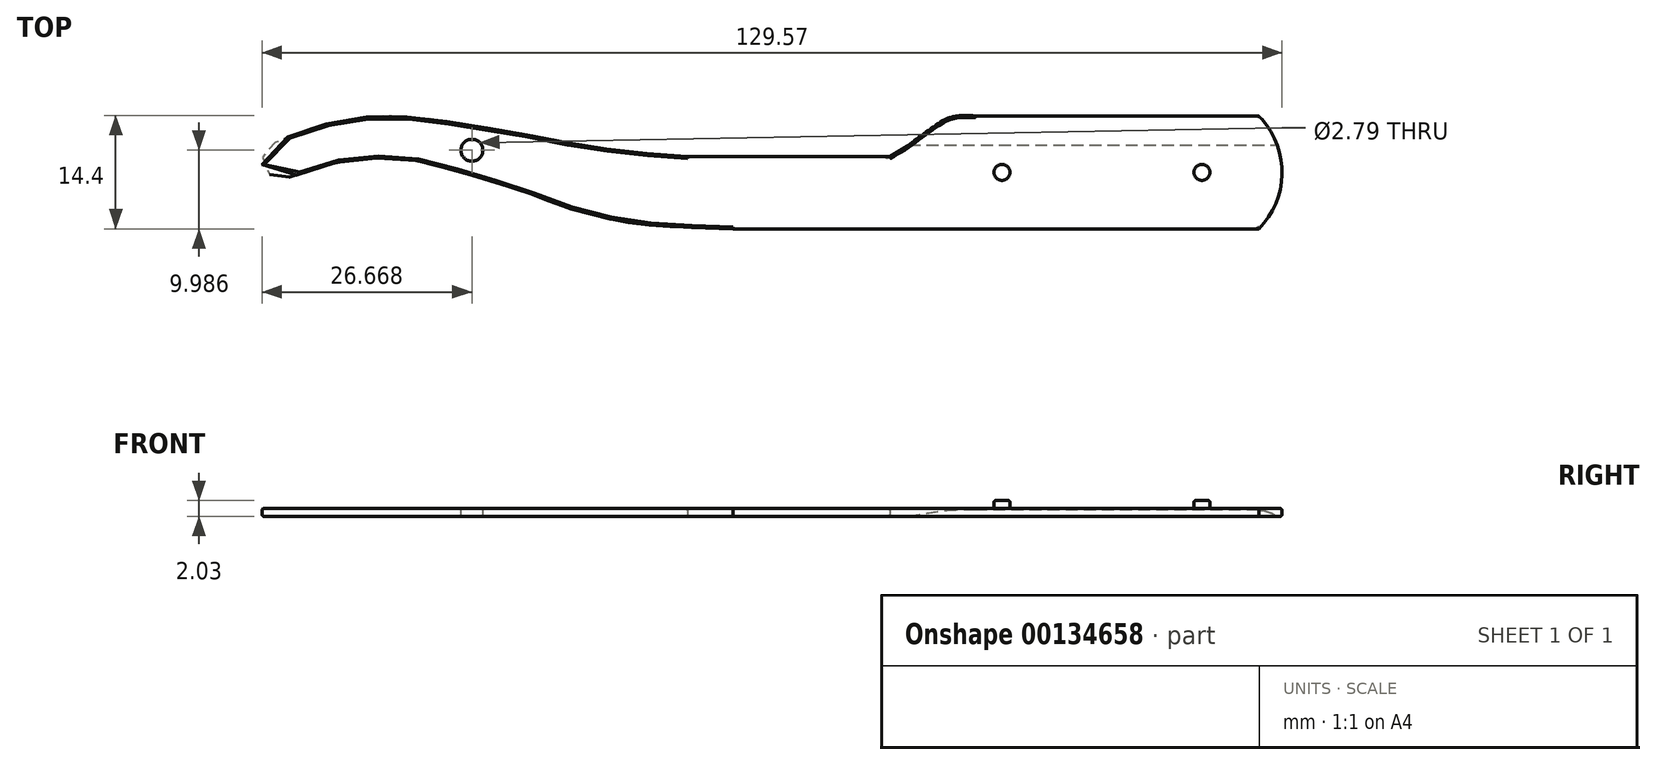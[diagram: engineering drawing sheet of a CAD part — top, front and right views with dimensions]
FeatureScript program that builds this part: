
annotation { "Feature Type Name" : "Feature", "Feature Type Description" : "" }
export const myFeature = defineFeature(function(context is Context, id is Id, definition is map)
    precondition{}
    {
        {
            var Q0;
            Q0=qCreatedBy(makeId("Top.planeOp"),FACE);
            var sketch = newSketch(context, id + "F0", { "sketchPlane" : qUnion([Q0])});
            skPoint(sketch, "E0", {"position": v(130.8, 0) * mm});
            skPoint(sketch, "E1", {"position": v(-103.94, -143.52) * mm});
            skPoint(sketch, "E2", {"position": v(0.55, 0.24) * mm});
            skPoint(sketch, "E3", {"position": v(0.4, 1.22) * mm});
            skPoint(sketch, "E4", {"position": v(0.7, 2.2) * mm});
            skPoint(sketch, "E5", {"position": v(1.36, 2.96) * mm});
            skPoint(sketch, "E6", {"position": v(5, 4.63) * mm});
            skPoint(sketch, "E7", {"position": v(9.58, 5.96) * mm});
            skPoint(sketch, "E8", {"position": v(14.71, 6.72) * mm});
            skPoint(sketch, "E9", {"position": v(19.41, 6.61) * mm});
            skPoint(sketch, "E10", {"position": v(22.67, 6.26) * mm});
            skPoint(sketch, "E11", {"position": v(23.56, 6.1) * mm});
            skPoint(sketch, "E12", {"position": v(33.06, 4.54) * mm});
            skPoint(sketch, "E13", {"position": v(37.97, 3.6) * mm});
            skPoint(sketch, "E14", {"position": v(42.95, 2.72) * mm});
            skPoint(sketch, "E15", {"position": v(46.9, 2.26) * mm});
            skPoint(sketch, "E16", {"position": v(51.6, 1.8) * mm});
            skPoint(sketch, "E17", {"position": v(54.47, 1.63) * mm});
            skPoint(sketch, "E18", {"position": v(80.16, 1.63) * mm});
            skPoint(sketch, "E19", {"position": v(82.68, 3.16) * mm});
            skPoint(sketch, "E20", {"position": v(83.83, 4.04) * mm});
            skPoint(sketch, "E21", {"position": v(85.06, 4.93) * mm});
            skPoint(sketch, "E22", {"position": v(86.43, 5.87) * mm});
            skPoint(sketch, "E23", {"position": v(87.8, 6.58) * mm});
            skPoint(sketch, "E24", {"position": v(89.43, 6.85) * mm});
            skPoint(sketch, "E25", {"position": v(91.29, 6.78) * mm});
            skPoint(sketch, "E26", {"position": v(127.01, 6.78) * mm});
            skPoint(sketch, "E27", {"position": v(128.33, 5.87) * mm});
            skPoint(sketch, "E28", {"position": v(129.3, 4.49) * mm});
            skPoint(sketch, "E29", {"position": v(130.18, 1.72) * mm});
            skPoint(sketch, "E30", {"position": v(130.35, -0.84) * mm});
            skPoint(sketch, "E31", {"position": v(129.95, -2.76) * mm});
            skPoint(sketch, "E32", {"position": v(128.97, -5.52) * mm});
            skPoint(sketch, "E33", {"position": v(127.42, -7.1) * mm});
            skPoint(sketch, "E34", {"position": v(127.01, -7.57) * mm});
            skPoint(sketch, "E35", {"position": v(60.22, -7.57) * mm});
            skPoint(sketch, "E36", {"position": v(53.63, -7.32) * mm});
            skPoint(sketch, "E37", {"position": v(47.48, -6.84) * mm});
            skPoint(sketch, "E38", {"position": v(41.94, -5.64) * mm});
            skPoint(sketch, "E39", {"position": v(38.32, -4.6) * mm});
            skPoint(sketch, "E40", {"position": v(34.93, -3.26) * mm});
            skPoint(sketch, "E41", {"position": v(22.9, 0.41) * mm});
            skPoint(sketch, "E42", {"position": v(19.37, 1.23) * mm});
            skPoint(sketch, "E43", {"position": v(15.74, 1.42) * mm});
            skPoint(sketch, "E44", {"position": v(11.4, 1.13) * mm});
            skPoint(sketch, "E45", {"position": v(8.54, 0.52) * mm});
            skPoint(sketch, "E46", {"position": v(5.77, 0) * mm});
            skPoint(sketch, "E47", {"position": v(4.05, -0.96) * mm});
            skPoint(sketch, "E48", {"position": v(2.62, -1.15) * mm});
            skPoint(sketch, "E49", {"position": v(1.82, -0.96) * mm});
            skPoint(sketch, "E50", {"position": v(1.25, -0.57) * mm});
            skPoint(sketch, "E51", {"position": v(0.81, -0.18) * mm});
            skLineSegment(sketch, "E52", {"start": v(91.29, 6.78) * mm, "end": v(127.01, 6.78) * mm});
            skLineSegment(sketch, "E53", {"start": v(60.22, -7.57) * mm, "end": v(127.01, -7.57) * mm});
            skLineSegment(sketch, "E54", {"start": v(54.47, 1.63) * mm, "end": v(80.16, 1.63) * mm});
            skFitSpline(sketch, "E55", {"points": [v(80.16, 1.63) * mm, v(82.68, 3.16) * mm, v(83.83, 4.04) * mm, v(85.06, 4.93) * mm, v(86.43, 5.87) * mm, v(87.8, 6.58) * mm, v(89.43, 6.85) * mm, v(91.29, 6.78) * mm], "startDerivative": vector(15.23, 8.8) * mm, "endDerivative": vector(12.83, -0.9) * mm});
            skArc(sketch, "E56", {"start": v(127.01, -7.57) * mm, "mid": v(129.97, -0.4) * mm, "end": v(127.01, 6.78) * mm});
            skFitSpline(sketch, "E57", {"points": [v(60.22, -7.57) * mm, v(53.63, -7.32) * mm, v(47.48, -6.84) * mm, v(41.94, -5.64) * mm, v(38.32, -4.6) * mm, v(34.93, -3.26) * mm, v(22.9, 0.41) * mm, v(19.37, 1.23) * mm, v(15.74, 1.42) * mm, v(11.4, 1.13) * mm, v(8.54, 0.52) * mm, v(4.05, -0.96) * mm, v(2.62, -1.15) * mm, v(1.82, -0.96) * mm, v(1.25, -0.57) * mm, v(0.81, -0.18) * mm, v(0.55, 0.24) * mm, v(0.4, 1.22) * mm, v(0.7, 2.2) * mm, v(1.36, 2.96) * mm, v(5, 4.63) * mm, v(9.58, 5.96) * mm, v(14.71, 6.72) * mm, v(19.41, 6.61) * mm, v(22.67, 6.26) * mm, v(23.56, 6.1) * mm, v(33.06, 4.54) * mm, v(37.97, 3.6) * mm, v(42.95, 2.72) * mm, v(46.9, 2.26) * mm, v(51.6, 1.8) * mm, v(54.47, 1.63) * mm], "startDerivative": vector(-147, 5.5) * mm, "endDerivative": vector(89.1, -4.43) * mm});
            skSolve(sketch);
        }
        {
            var Q0;
            Q0 = qSketchRegion(id + "F0", true);
            extrude(context, id + "F1", {"entities" : qUnion([Q0]), "depth" : 1.02 * mm});
        }
        {
            var Q0;
            Q0=makeQuery(id+"F1.opExtrude","CAP_FACE",FACE,{"disambiguationData":[OSD([sQuery(id+"F0.wireOp",EDGE,"E52"),sQuery(id+"F0.wireOp",EDGE,"E53"),sQuery(id+"F0.wireOp",EDGE,"E54"),sQuery(id+"F0.wireOp",EDGE,"E55"),sQuery(id+"F0.wireOp",EDGE,"E56"),sQuery(id+"F0.wireOp",EDGE,"E57")])],"isStart":false});
            var sketch = newSketch(context, id + "F2", { "sketchPlane" : qUnion([Q0])});
            skCircle(sketch, "E58", {"center": v(119.81, -0.4) * mm, "radius": 1.02 * mm});
            skPoint(sketch, "E58.centerSnap0", {"position": v(129.97, -0.4) * mm});
            skCircle(sketch, "E59", {"center": v(94.41, -0.4) * mm, "radius": 1.02 * mm});
            skSolve(sketch);
        }
        {
            var Q0;
            Q0=makeQuery(id+"F2.imprint","IMPRINT",FACE,{"disambiguationData":[TD([[makeQuery(id+"F2.imprint","IMPRINT",EDGE,{"derivedFrom":sQuery(id+"F2.wireOp",EDGE,"E58")}),-1.0]])]});
            var sketch = newSketch(context, id + "F3", { "sketchPlane" : qUnion([Q0])});
            skCircle(sketch, "E60", {"center": v(27.07, 2.42) * mm, "radius": 1.4 * mm});
            skPoint(sketch, "E61", {"position": v(0.4, 1.03) * mm});
            skSolve(sketch);
        }
        {
            var Q0;
            Q0 = qSketchRegion(id + "F3", true);
            extrude(context, id + "F4", {"entities" : qUnion([Q0]), "operationType" : NewBodyOperationType.REMOVE, "endBound" : BoundingType.THROUGH_ALL, "oppositeDirection" : true, "depth" : 25.4 * mm});
        }
        {
            var Q0;
            Q0 = qSketchRegion(id + "F2", true);
            extrude(context, id + "F5", {"entities" : qUnion([Q0]), "operationType" : NewBodyOperationType.ADD, "depth" : 1.02 * mm});
        }
        {
            var Q0;
            Q0=qCreatedBy(makeId("Right.planeOp"),FACE);
            cPlane(context, id + "F6", {"entities" : qUnion([Q0]), "cplaneType" : CPlaneType.OFFSET, "offset" : 152.4 * mm, "width" : 152.4 * mm, "height" : 152.4 * mm});
        }
        {
            var Q0;
            Q0=qCreatedBy(id+"F6.planeOp",FACE);
            var sketch = newSketch(context, id + "F7", { "sketchPlane" : qUnion([Q0])});
            skLineSegment(sketch, "E62", {"start": v(6.87, 0) * mm, "end": v(6.87, 0.88) * mm});
            skLineSegment(sketch, "E63", {"start": v(6.87, 0.88) * mm, "end": v(3.06, 0) * mm});
            skLineSegment(sketch, "E64", {"start": v(3.06, 0) * mm, "end": v(6.87, 0) * mm});
            skSolve(sketch);
        }
        {
            var Q0;
            Q0 = qSketchRegion(id + "F7", true);
            extrude(context, id + "F8", {"entities" : qUnion([Q0]), "operationType" : NewBodyOperationType.REMOVE, "oppositeDirection" : true, "depth" : 73.66 * mm});
        }
        {
            var Q0;
            Q0=makeQuery(id+"F1.opExtrude","CAP_EDGE",EDGE,{"disambiguationData":[OSD([sQuery(id+"F0.wireOp",EDGE,"E57")])],"isStart":false});
            var Q1;
            Q1=makeQuery(id+"F1.opExtrude","CAP_EDGE",EDGE,{"disambiguationData":[OSD([sQuery(id+"F0.wireOp",EDGE,"E54")])],"isStart":false});
            var Q2;
            Q2=makeQuery(id+"F1.opExtrude","CAP_EDGE",EDGE,{"disambiguationData":[OSD([sQuery(id+"F0.wireOp",EDGE,"E54")])],"isStart":true});
            var Q3;
            Q3=makeQuery(id+"F1.opExtrude","CAP_EDGE",EDGE,{"disambiguationData":[OSD([sQuery(id+"F0.wireOp",EDGE,"E53")])],"isStart":false});
            var Q4;
            Q4=makeQuery(id+"F1.opExtrude","CAP_EDGE",EDGE,{"disambiguationData":[OSD([sQuery(id+"F0.wireOp",EDGE,"E53")])],"isStart":true});
            var Q5;
            Q5=makeQuery(id+"F1.opExtrude","CAP_EDGE",EDGE,{"disambiguationData":[OSD([sQuery(id+"F0.wireOp",EDGE,"E57")])],"isStart":true});
            var Q6;
            Q6=makeQuery(id+"F1.opExtrude","CAP_EDGE",EDGE,{"disambiguationData":[OSD([sQuery(id+"F0.wireOp",EDGE,"E56")])],"isStart":false});
            var Q7;
            Q7=makeQuery(id+"F1.opExtrude","CAP_EDGE",EDGE,{"disambiguationData":[OSD([sQuery(id+"F0.wireOp",EDGE,"E56")])],"isStart":true});
            var Q8;
            Q8=makeQuery(id+"F1.opExtrude","CAP_EDGE",EDGE,{"disambiguationData":[OSD([sQuery(id+"F0.wireOp",EDGE,"E52")])],"isStart":false});
            var Q9;
            Q9=makeQuery(id+"F1.opExtrude","CAP_EDGE",EDGE,{"disambiguationData":[OSD([sQuery(id+"F0.wireOp",EDGE,"E55")])],"isStart":false});
            var Q10;
            Q10=makeQuery(id+"F5.opExtrude","SWEPT_FACE",FACE,{"disambiguationData":[OSD([sQuery(id+"F2.wireOp",EDGE,"E59")])]});
            var Q11;
            Q11=makeQuery(id+"F5.opExtrude","SWEPT_FACE",FACE,{"disambiguationData":[OSD([sQuery(id+"F2.wireOp",EDGE,"E58")])]});
            fillet(context, id + "F9", {"entities" : qUnion([Q0, Q1, Q2, Q3, Q4, Q5, Q6, Q7, Q8, Q9, Q10, Q11]), "radius" : 0.25 * mm, "tangentPropagation" : true, "allowEdgeOverflow" : false});
        }
    });
